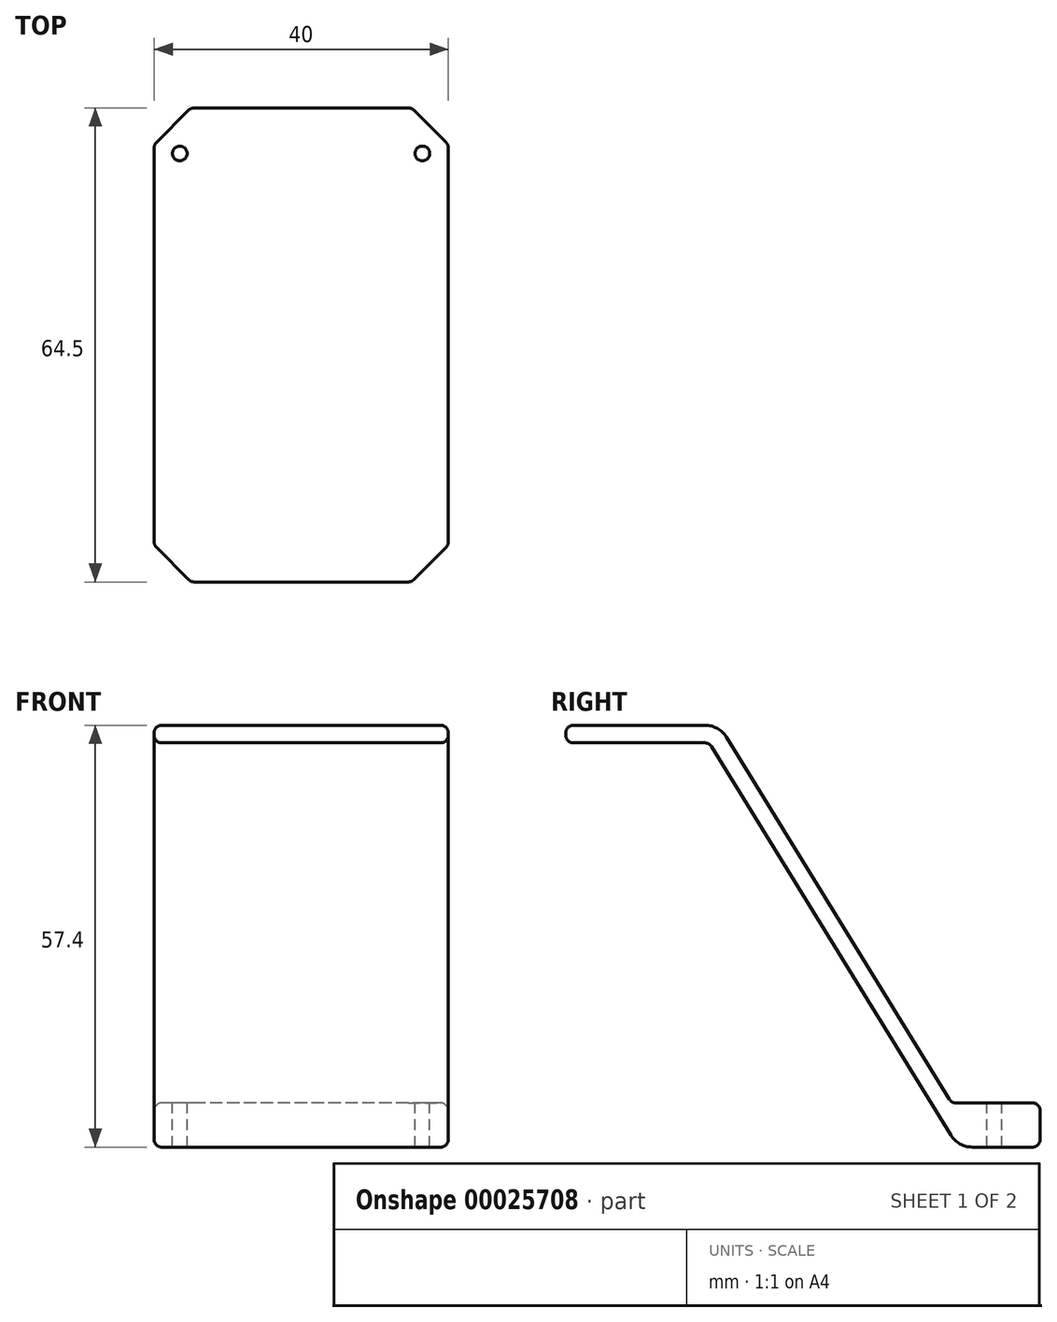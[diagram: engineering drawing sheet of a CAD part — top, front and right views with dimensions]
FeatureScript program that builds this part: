
annotation { "Feature Type Name" : "Feature", "Feature Type Description" : "" }
export const myFeature = defineFeature(function(context is Context, id is Id, definition is map)
    precondition{}
    {
        {
            var Q0;
            Q0=qCreatedBy(makeId("Right.planeOp"),FACE);
            var sketch = newSketch(context, id + "F0", { "sketchPlane" : qUnion([Q0])});
            skLineSegment(sketch, "E0", {"start": v(0, 0) * mm, "end": v(12, 0) * mm});
            skLineSegment(sketch, "E1", {"start": v(12, 0) * mm, "end": v(12, -6) * mm});
            skLineSegment(sketch, "E2", {"start": v(12, -6) * mm, "end": v(0.88, -6) * mm});
            skLineSegment(sketch, "E3", {"start": v(0.88, -6) * mm, "end": v(-33, 49) * mm});
            skLineSegment(sketch, "E4", {"start": v(-33, 49) * mm, "end": v(-52.5, 49) * mm});
            skLineSegment(sketch, "E5", {"start": v(-52.5, 49) * mm, "end": v(-52.5, 51.4) * mm});
            skLineSegment(sketch, "E6", {"start": v(-52.5, 51.4) * mm, "end": v(-31.66, 51.4) * mm});
            skLineSegment(sketch, "E7", {"start": v(-31.66, 51.4) * mm, "end": v(0, 0) * mm});
            skSolve(sketch);
        }
        {
            var Q0;
            Q0 = qSketchRegion(id + "F0", true);
            extrude(context, id + "F1", {"entities" : qUnion([Q0]), "depth" : 40 * mm});
        }
        {
            var Q0;
            Q0=makeQuery(id+"F1.opExtrude","SWEPT_FACE",FACE,{"disambiguationData":[OSD([sQuery(id+"F0.wireOp",EDGE,"E0")])]});
            var sketch = newSketch(context, id + "F2", { "sketchPlane" : qUnion([Q0])});
            skCircle(sketch, "E8", {"center": v(3.48, 5.8) * mm, "radius": 1 * mm});
            skCircle(sketch, "E9", {"center": v(36.48, 5.8) * mm, "radius": 1 * mm});
            skLineSegment(sketch, "E10", {"start": v(3.48, 5.8) * mm, "end": v(36.48, 5.8) * mm, "construction": true});
            skLineSegment(sketch, "E11", {"start": v(19.98, 5.8) * mm, "end": v(19.98, 12) * mm, "construction": true});
            skSolve(sketch);
        }
        {
            var Q0;
            Q0 = qSketchRegion(id + "F2", true);
            extrude(context, id + "F3", {"entities" : qUnion([Q0]), "operationType" : NewBodyOperationType.REMOVE, "oppositeDirection" : true, "depth" : 25 * mm});
        }
        {
            var Q0;
            Q0=makeQuery(id+"F1.opExtrude","SWEPT_EDGE",EDGE,{"disambiguationData":[OSD([sQuery(id+"F0.wireOp",EDGE,"E0"),sQuery(id+"F0.wireOp",EDGE,"E7")])]});
            var Q1;
            Q1=makeQuery(id+"F1.opExtrude","SWEPT_EDGE",EDGE,{"disambiguationData":[OSD([sQuery(id+"F0.wireOp",EDGE,"E3"),sQuery(id+"F0.wireOp",EDGE,"E4")])]});
            fillet(context, id + "F4", {"entities" : qUnion([Q0, Q1]), "radius" : 1 * mm, "tangentPropagation" : true, "allowEdgeOverflow" : false});
        }
        {
            var Q0;
            Q0=makeQuery(id+"F1.opExtrude","SWEPT_EDGE",EDGE,{"disambiguationData":[OSD([sQuery(id+"F0.wireOp",EDGE,"E6"),sQuery(id+"F0.wireOp",EDGE,"E7")])]});
            var Q1;
            Q1=makeQuery(id+"F1.opExtrude","SWEPT_EDGE",EDGE,{"disambiguationData":[OSD([sQuery(id+"F0.wireOp",EDGE,"E2"),sQuery(id+"F0.wireOp",EDGE,"E3")])]});
            fillet(context, id + "F5", {"entities" : qUnion([Q0, Q1]), "radius" : 3.4 * mm, "tangentPropagation" : true, "allowEdgeOverflow" : false});
        }
        {
            var Q0;
            Q0=makeQuery(id+"F1.opExtrude","CAP_EDGE",EDGE,{"disambiguationData":[OSD([sQuery(id+"F0.wireOp",EDGE,"E5")])],"isStart":false});
            var Q1;
            Q1=makeQuery(id+"F1.opExtrude","CAP_EDGE",EDGE,{"disambiguationData":[OSD([sQuery(id+"F0.wireOp",EDGE,"E1")])],"isStart":false});
            var Q2;
            Q2=makeQuery(id+"F1.opExtrude","CAP_EDGE",EDGE,{"disambiguationData":[OSD([sQuery(id+"F0.wireOp",EDGE,"E5")])],"isStart":true});
            var Q3;
            Q3=makeQuery(id+"F1.opExtrude","CAP_EDGE",EDGE,{"disambiguationData":[OSD([sQuery(id+"F0.wireOp",EDGE,"E1")])],"isStart":true});
            chamfer(context, id + "F6", {"entities" : qUnion([Q0, Q1, Q2, Q3]), "width" : 5 * mm, "tangentPropagation" : true});
        }
        {
            var Q0;
            {var subQ0=sQuery(id+"F0.wireOp",EDGE,"E1");Q0=makeQuery(id+"F6.opChamfer","BLEND_EDGE",EDGE,{"blendedFrom":[makeQuery(id+"F1.opExtrude","CAP_EDGE",EDGE,{"disambiguationData":[OSD([subQ0])],"isStart":true}),makeQuery(id+"F1.opExtrude","SWEPT_FACE",FACE,{"disambiguationData":[OSD([subQ0])]})],"blendedInto":[makeQuery(id+"F1.opExtrude","SWEPT_FACE",FACE,{"disambiguationData":[OSD([subQ0])]})]});}
            var Q1;
            {var subQ0=sQuery(id+"F0.wireOp",EDGE,"E1");Q1=makeQuery(id+"F6.opChamfer","BLEND_EDGE",EDGE,{"blendedFrom":[makeQuery(id+"F1.opExtrude","CAP_EDGE",EDGE,{"disambiguationData":[OSD([subQ0])],"isStart":false}),makeQuery(id+"F1.opExtrude","SWEPT_FACE",FACE,{"disambiguationData":[OSD([subQ0])]})],"blendedInto":[makeQuery(id+"F1.opExtrude","SWEPT_FACE",FACE,{"disambiguationData":[OSD([subQ0])]})]});}
            var Q2;
            {var subQ0=sQuery(id+"F0.wireOp",EDGE,"E5");Q2=makeQuery(id+"F6.opChamfer","BLEND_EDGE",EDGE,{"blendedFrom":[makeQuery(id+"F1.opExtrude","CAP_EDGE",EDGE,{"disambiguationData":[OSD([subQ0])],"isStart":false}),makeQuery(id+"F1.opExtrude","SWEPT_FACE",FACE,{"disambiguationData":[OSD([subQ0])]})],"blendedInto":[makeQuery(id+"F1.opExtrude","SWEPT_FACE",FACE,{"disambiguationData":[OSD([subQ0])]})]});}
            var Q3;
            {var subQ0=sQuery(id+"F0.wireOp",EDGE,"E5");Q3=makeQuery(id+"F6.opChamfer","BLEND_EDGE",EDGE,{"blendedFrom":[makeQuery(id+"F1.opExtrude","CAP_EDGE",EDGE,{"disambiguationData":[OSD([subQ0])],"isStart":true}),makeQuery(id+"F1.opExtrude","SWEPT_FACE",FACE,{"disambiguationData":[OSD([subQ0])]})],"blendedInto":[makeQuery(id+"F1.opExtrude","SWEPT_FACE",FACE,{"disambiguationData":[OSD([subQ0])]})]});}
            fillet(context, id + "F7", {"entities" : qUnion([Q0, Q1, Q2, Q3]), "radius" : 1 * mm, "tangentPropagation" : true, "allowEdgeOverflow" : false});
        }
        {
            var Q0;
            {var subQ0=sQuery(id+"F0.wireOp",EDGE,"E5");Q0=makeQuery(id+"F6.opChamfer","BLEND_EDGE",EDGE,{"blendedFrom":[makeQuery(id+"F1.opExtrude","CAP_EDGE",EDGE,{"disambiguationData":[OSD([subQ0])],"isStart":true}),makeQuery(id+"F1.opExtrude","CAP_FACE",FACE,{"disambiguationData":[OSD([sQuery(id+"F0.wireOp",EDGE,"E0"),sQuery(id+"F0.wireOp",EDGE,"E1"),sQuery(id+"F0.wireOp",EDGE,"E2"),sQuery(id+"F0.wireOp",EDGE,"E3"),sQuery(id+"F0.wireOp",EDGE,"E4"),subQ0,sQuery(id+"F0.wireOp",EDGE,"E6"),sQuery(id+"F0.wireOp",EDGE,"E7")])],"isStart":true})],"blendedInto":[makeQuery(id+"F1.opExtrude","CAP_FACE",FACE,{"disambiguationData":[OSD([sQuery(id+"F0.wireOp",EDGE,"E0"),sQuery(id+"F0.wireOp",EDGE,"E1"),sQuery(id+"F0.wireOp",EDGE,"E2"),sQuery(id+"F0.wireOp",EDGE,"E3"),sQuery(id+"F0.wireOp",EDGE,"E4"),subQ0,sQuery(id+"F0.wireOp",EDGE,"E6"),sQuery(id+"F0.wireOp",EDGE,"E7")])],"isStart":true})]});}
            var Q1;
            {var subQ0=sQuery(id+"F0.wireOp",EDGE,"E1");Q1=makeQuery(id+"F6.opChamfer","BLEND_EDGE",EDGE,{"blendedFrom":[makeQuery(id+"F1.opExtrude","CAP_EDGE",EDGE,{"disambiguationData":[OSD([subQ0])],"isStart":true}),makeQuery(id+"F1.opExtrude","CAP_FACE",FACE,{"disambiguationData":[OSD([sQuery(id+"F0.wireOp",EDGE,"E0"),subQ0,sQuery(id+"F0.wireOp",EDGE,"E2"),sQuery(id+"F0.wireOp",EDGE,"E3"),sQuery(id+"F0.wireOp",EDGE,"E4"),sQuery(id+"F0.wireOp",EDGE,"E5"),sQuery(id+"F0.wireOp",EDGE,"E6"),sQuery(id+"F0.wireOp",EDGE,"E7")])],"isStart":true})],"blendedInto":[makeQuery(id+"F1.opExtrude","CAP_FACE",FACE,{"disambiguationData":[OSD([sQuery(id+"F0.wireOp",EDGE,"E0"),subQ0,sQuery(id+"F0.wireOp",EDGE,"E2"),sQuery(id+"F0.wireOp",EDGE,"E3"),sQuery(id+"F0.wireOp",EDGE,"E4"),sQuery(id+"F0.wireOp",EDGE,"E5"),sQuery(id+"F0.wireOp",EDGE,"E6"),sQuery(id+"F0.wireOp",EDGE,"E7")])],"isStart":true})]});}
            var Q2;
            {var subQ0=sQuery(id+"F0.wireOp",EDGE,"E1");Q2=makeQuery(id+"F6.opChamfer","BLEND_EDGE",EDGE,{"blendedFrom":[makeQuery(id+"F1.opExtrude","CAP_EDGE",EDGE,{"disambiguationData":[OSD([subQ0])],"isStart":false}),makeQuery(id+"F1.opExtrude","CAP_FACE",FACE,{"disambiguationData":[OSD([sQuery(id+"F0.wireOp",EDGE,"E0"),subQ0,sQuery(id+"F0.wireOp",EDGE,"E2"),sQuery(id+"F0.wireOp",EDGE,"E3"),sQuery(id+"F0.wireOp",EDGE,"E4"),sQuery(id+"F0.wireOp",EDGE,"E5"),sQuery(id+"F0.wireOp",EDGE,"E6"),sQuery(id+"F0.wireOp",EDGE,"E7")])],"isStart":false})],"blendedInto":[makeQuery(id+"F1.opExtrude","CAP_FACE",FACE,{"disambiguationData":[OSD([sQuery(id+"F0.wireOp",EDGE,"E0"),subQ0,sQuery(id+"F0.wireOp",EDGE,"E2"),sQuery(id+"F0.wireOp",EDGE,"E3"),sQuery(id+"F0.wireOp",EDGE,"E4"),sQuery(id+"F0.wireOp",EDGE,"E5"),sQuery(id+"F0.wireOp",EDGE,"E6"),sQuery(id+"F0.wireOp",EDGE,"E7")])],"isStart":false})]});}
            var Q3;
            {var subQ0=sQuery(id+"F0.wireOp",EDGE,"E5");Q3=makeQuery(id+"F6.opChamfer","BLEND_EDGE",EDGE,{"blendedFrom":[makeQuery(id+"F1.opExtrude","CAP_EDGE",EDGE,{"disambiguationData":[OSD([subQ0])],"isStart":false}),makeQuery(id+"F1.opExtrude","CAP_FACE",FACE,{"disambiguationData":[OSD([sQuery(id+"F0.wireOp",EDGE,"E0"),sQuery(id+"F0.wireOp",EDGE,"E1"),sQuery(id+"F0.wireOp",EDGE,"E2"),sQuery(id+"F0.wireOp",EDGE,"E3"),sQuery(id+"F0.wireOp",EDGE,"E4"),subQ0,sQuery(id+"F0.wireOp",EDGE,"E6"),sQuery(id+"F0.wireOp",EDGE,"E7")])],"isStart":false})],"blendedInto":[makeQuery(id+"F1.opExtrude","CAP_FACE",FACE,{"disambiguationData":[OSD([sQuery(id+"F0.wireOp",EDGE,"E0"),sQuery(id+"F0.wireOp",EDGE,"E1"),sQuery(id+"F0.wireOp",EDGE,"E2"),sQuery(id+"F0.wireOp",EDGE,"E3"),sQuery(id+"F0.wireOp",EDGE,"E4"),subQ0,sQuery(id+"F0.wireOp",EDGE,"E6"),sQuery(id+"F0.wireOp",EDGE,"E7")])],"isStart":false})]});}
            fillet(context, id + "F8", {"entities" : qUnion([Q0, Q1, Q2, Q3]), "radius" : 1 * mm, "tangentPropagation" : true, "allowEdgeOverflow" : false});
        }
        {
            var Q0;
            Q0=makeQuery(id+"F1.opExtrude","CAP_EDGE",EDGE,{"disambiguationData":[OSD([sQuery(id+"F0.wireOp",EDGE,"E4")])],"isStart":false});
            var Q1;
            Q1=makeQuery(id+"F1.opExtrude","CAP_EDGE",EDGE,{"disambiguationData":[OSD([sQuery(id+"F0.wireOp",EDGE,"E6")])],"isStart":false});
            fillet(context, id + "F9", {"entities" : qUnion([Q0, Q1]), "radius" : 1 * mm, "tangentPropagation" : true, "allowEdgeOverflow" : false});
        }
    });
